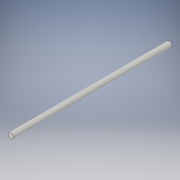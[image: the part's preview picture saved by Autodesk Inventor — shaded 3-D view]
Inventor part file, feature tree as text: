
AUTODESK INVENTOR PART (.ipt)
format: ipt  version: 2017 (Build 210142000, 142)  size: 89,088 bytes
history: native  units: in
note: dims shown in document units (in); Inventor stores cm internally (conversion verified against a paired STEP export)
features: extrude x1, sketch x1
ambient origin geometry x8: Origin, YZ Plane, XZ Plane, XY Plane, X Axis, Y Axis, Z Axis, Center Point
bodies: Solid1 (feature_tree)
feature tree (2):
  extrude  "Extrusion1"  Depth=3.45in TaperAngle=0.0deg
  sketch  "Sketch1"  dims[d0=0.1181in d1=3.45in d2=0.0in]
